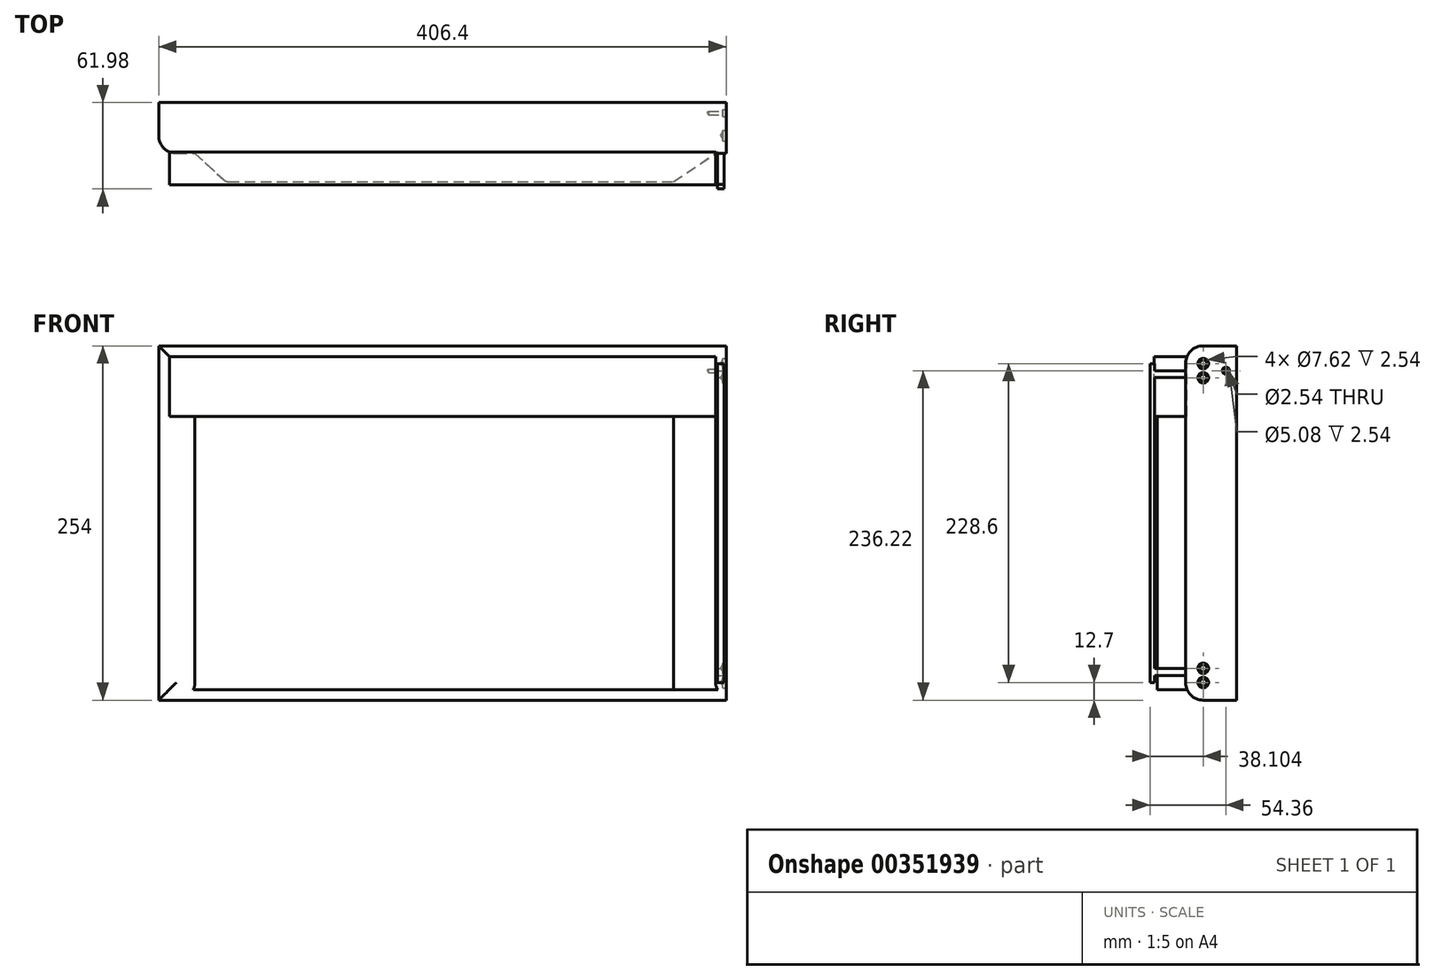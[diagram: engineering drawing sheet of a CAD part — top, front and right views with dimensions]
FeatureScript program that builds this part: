
annotation { "Feature Type Name" : "Feature", "Feature Type Description" : "" }
export const myFeature = defineFeature(function(context is Context, id is Id, definition is map)
    precondition{}
    {
        {
            var Q0;
            Q0=qCreatedBy(makeId("Front.planeOp"),FACE);
            var sketch = newSketch(context, id + "F0", { "sketchPlane" : qUnion([Q0])});
            skLineSegment(sketch, "E0.bottom", {"start": v(0, 0) * mm, "end": v(-406.4, 0) * mm});
            skLineSegment(sketch, "E0.top", {"start": v(0, -254) * mm, "end": v(-406.4, -254) * mm});
            skLineSegment(sketch, "E0.left", {"start": v(0, 0) * mm, "end": v(0, -254) * mm});
            skLineSegment(sketch, "E0.right", {"start": v(-406.4, 0) * mm, "end": v(-406.4, -254) * mm});
            skSolve(sketch);
        }
        {
            var Q0;
            Q0=makeQuery(id+"F0.imprint","IMPRINT",FACE,{"disambiguationData":[TD([[makeQuery(id+"F0.imprint","IMPRINT",EDGE,{"derivedFrom":sQuery(id+"F0.wireOp",EDGE,"E0.bottom")}),1.0]])]});
            extrude(context, id + "F1", {"entities" : qUnion([Q0]), "depth" : 36.58 * mm});
        }
        {
            var Q0;
            Q0=makeQuery(id+"F1.opExtrude","CAP_FACE",FACE,{"disambiguationData":[OSD([sQuery(id+"F0.wireOp",EDGE,"E0.bottom"),sQuery(id+"F0.wireOp",EDGE,"E0.top"),sQuery(id+"F0.wireOp",EDGE,"E0.left"),sQuery(id+"F0.wireOp",EDGE,"E0.right")])],"isStart":false});
            var sketch = newSketch(context, id + "F2", { "sketchPlane" : qUnion([Q0])});
            skLineSegment(sketch, "E1", {"start": v(-398.78, -246.38) * mm, "end": v(-398.78, -7.62) * mm});
            skLineSegment(sketch, "E2", {"start": v(-398.78, -7.62) * mm, "end": v(-7.62, -7.62) * mm});
            skLineSegment(sketch, "E3", {"start": v(-398.78, -246.38) * mm, "end": v(-7.62, -246.38) * mm});
            skLineSegment(sketch, "E4", {"start": v(-7.62, -246.38) * mm, "end": v(-7.62, -7.62) * mm});
            skSolve(sketch);
        }
        {
            var Q0;
            Q0=makeQuery(id+"F2.imprint","IMPRINT",FACE,{"disambiguationData":[TD([[makeQuery(id+"F2.imprint","IMPRINT",EDGE,{"derivedFrom":sQuery(id+"F2.wireOp",EDGE,"E1")}),-1.0]])]});
            extrude(context, id + "F3", {"entities" : qUnion([Q0]), "operationType" : NewBodyOperationType.ADD, "depth" : 22.6 * mm});
        }
        {
            var Q0;
            Q0=makeQuery(id+"F3.opExtrude","SWEPT_FACE",FACE,{"disambiguationData":[OSD([sQuery(id+"F2.wireOp",EDGE,"E3")])]});
            var sketch = newSketch(context, id + "F4", { "sketchPlane" : qUnion([Q0])});
            skLineSegment(sketch, "E5", {"start": v(-380.42, 36.58) * mm, "end": v(-358.27, 56.85) * mm});
            skLineSegment(sketch, "E6", {"start": v(-358.27, 56.85) * mm, "end": v(-37.8, 56.85) * mm});
            skLineSegment(sketch, "E7", {"start": v(-37.8, 56.85) * mm, "end": v(-7.62, 36.58) * mm});
            skSolve(sketch);
        }
        {
            var Q0;
            {var subQ2=sQuery(id+"F4.wireOp",EDGE,"E5");Q0=makeQuery(id+"F4.imprint","IMPRINT",FACE,{"disambiguationData":[TD([[makeQuery(id+"F4.imprint","IMPRINT",EDGE,{"derivedFrom":subQ2}),1.0]])]});}
            extrude(context, id + "F5", {"entities" : qUnion([Q0]), "operationType" : NewBodyOperationType.REMOVE, "oppositeDirection" : true, "depth" : 195.83 * mm});
        }
        {
            var Q0;
            Q0=makeQuery(id+"F5.boolean.opBoolean","COPY",EDGE,{"derivedFrom":makeQuery(id+"F5.opExtrude","CAP_EDGE",EDGE,{"disambiguationData":[OSD([sQuery(id+"F4.wireOp",EDGE,"E6")])],"isStart":true})});
            var Q1;
            Q1=makeQuery(id+"F5.boolean.opBoolean","COPY",EDGE,{"derivedFrom":makeQuery(id+"F5.opExtrude","CAP_EDGE",EDGE,{"disambiguationData":[OSD([sQuery(id+"F4.wireOp",EDGE,"E5")])],"isStart":true})});
            var Q2;
            Q2=makeQuery(id+"F5.boolean.opBoolean","COPY",EDGE,{"derivedFrom":makeQuery(id+"F5.opExtrude","SWEPT_EDGE",EDGE,{"disambiguationData":[OSD([sQuery(id+"F4.wireOp",EDGE,"E5"),sQuery(id+"F4.wireOp",EDGE,"E6")])]})});
            var Q3;
            Q3=makeQuery(id+"F5.boolean.opBoolean","INTERSECT",EDGE,{"derivedFrom":[makeQuery(id+"F3.opExtrude","SWEPT_FACE",FACE,{"disambiguationData":[OSD([sQuery(id+"F2.wireOp",EDGE,"E2")])]}),makeQuery(id+"F5.opExtrude","SWEPT_FACE",FACE,{"disambiguationData":[OSD([sQuery(id+"F4.wireOp",EDGE,"E5")])]})]});
            var Q4;
            Q4=makeQuery(id+"F5.boolean.opBoolean","INTERSECT",EDGE,{"derivedFrom":[makeQuery(id+"F3.opExtrude","SWEPT_FACE",FACE,{"disambiguationData":[OSD([sQuery(id+"F2.wireOp",EDGE,"E2")])]}),makeQuery(id+"F5.opExtrude","SWEPT_FACE",FACE,{"disambiguationData":[OSD([sQuery(id+"F4.wireOp",EDGE,"E6")])]})]});
            var Q5;
            {var subQ0=sQuery(id+"F7NSI61EkHc6LHw_1.wireOp",EDGE,"ORKUqMSw-jbk6-ItTb-sdrK-fpS0Z8fCi9uI");var subQ1=sQuery(id+"F7NSI61EkHc6LHw_1.wireOp",EDGE,"0TJsNva3-6Dh7-84AK-LeQ4-RBizLzSJ0fqv");var subQ2=sQuery(id+"F4.wireOp",EDGE,"E7");var subQ7=makeQuery(id+"F5.boolean.opBoolean","COPY",EDGE,{"derivedFrom":makeQuery(id+"F5.opExtrude","CAP_EDGE",EDGE,{"disambiguationData":[OSD([subQ2])],"isStart":true})});Q5=makeQuery(id+"FVFLB6VGkvuXAbx_1.boolean.opBoolean","MERGE",EDGE,{"derivedFrom":[makeQuery(id+"FeTA0CBMJBVCges_1.boolean.opBoolean","SPLIT",EDGE,{"disambiguationData":[TD([makeQuery(id+"FeTA0CBMJBVCges_1.opExtrude","SWEPT_FACE",FACE,{"disambiguationData":[OSD([subQ1])]})])],"derivedFrom":subQ7}),makeQuery(id+"FeTA0CBMJBVCges_1.boolean.opBoolean","SPLIT",EDGE,{"disambiguationData":[TD([makeQuery(id+"F5.boolean.opBoolean","COPY",FACE,{"derivedFrom":makeQuery(id+"F5.opExtrude","SWEPT_FACE",FACE,{"disambiguationData":[OSD([sQuery(id+"F4.wireOp",EDGE,"E6")])]})})])],"derivedFrom":subQ7}),makeQuery(id+"FVFLB6VGkvuXAbx_1.opExtrude","SWEPT_EDGE",EDGE,{"disambiguationData":[OSD([subQ2,subQ1,subQ0])]})]});}
            var Q6;
            {var subQ0=sQuery(id+"F7NSI61EkHc6LHw_1.wireOp",EDGE,"0TJsNva3-6Dh7-84AK-LeQ4-RBizLzSJ0fqv");var subQ1=sQuery(id+"F7NSI61EkHc6LHw_1.wireOp",EDGE,"UkR4Pr4L-OhKx-Odhu-bI6Y-4uwR8GJGrYWx");var subQ2=sQuery(id+"F4.wireOp",EDGE,"E7");var subQ3=sQuery(id+"F2.wireOp",EDGE,"E2");var subQ4=makeQuery(id+"F5.opExtrude","SWEPT_FACE",FACE,{"disambiguationData":[OSD([subQ2])]});var subQ6=makeQuery(id+"F3.opExtrude","SWEPT_FACE",FACE,{"disambiguationData":[OSD([subQ3])]});var subQ8=makeQuery(id+"F5.boolean.opBoolean","INTERSECT",EDGE,{"derivedFrom":[subQ6,subQ4]});Q6=makeQuery(id+"FVFLB6VGkvuXAbx_1.boolean.opBoolean","MERGE",EDGE,{"derivedFrom":[makeQuery(id+"FeTA0CBMJBVCges_1.boolean.opBoolean","SPLIT",EDGE,{"disambiguationData":[TD([makeQuery(id+"FeTA0CBMJBVCges_1.opExtrude","SWEPT_FACE",FACE,{"disambiguationData":[OSD([subQ0])]})])],"derivedFrom":subQ8}),makeQuery(id+"FeTA0CBMJBVCges_1.boolean.opBoolean","SPLIT",EDGE,{"disambiguationData":[TD([makeQuery(id+"F5.boolean.opBoolean","COPY",FACE,{"derivedFrom":makeQuery(id+"F5.opExtrude","SWEPT_FACE",FACE,{"disambiguationData":[OSD([sQuery(id+"F4.wireOp",EDGE,"E6")])]})})])],"derivedFrom":subQ8}),makeQuery(id+"FVFLB6VGkvuXAbx_1.opExtrude","SWEPT_EDGE",EDGE,{"disambiguationData":[OSD([subQ3,subQ2,subQ1,subQ0])]})]});}
            var Q7;
            Q7=makeQuery(id+"FeTA0CBMJBVCges_1.opExtrude","CAP_EDGE",EDGE,{"disambiguationData":[OSD([sQuery(id+"F7NSI61EkHc6LHw_1.wireOp",EDGE,"ORKUqMSw-jbk6-ItTb-sdrK-fpS0Z8fCi9uI")])],"isStart":false});
            var Q8;
            Q8=makeQuery(id+"FeTA0CBMJBVCges_1.opExtrude","CAP_EDGE",EDGE,{"disambiguationData":[OSD([sQuery(id+"F7NSI61EkHc6LHw_1.wireOp",EDGE,"UkR4Pr4L-OhKx-Odhu-bI6Y-4uwR8GJGrYWx")])],"isStart":false});
            var Q9;
            Q9=makeQuery(id+"FVFLB6VGkvuXAbx_1.boolean.opBoolean","COPY",EDGE,{"derivedFrom":makeQuery(id+"FVFLB6VGkvuXAbx_1.opExtrude","CAP_EDGE",EDGE,{"disambiguationData":[OSD([sQuery(id+"FHyrUoYh2R4RpAu_1.wireOp",EDGE,"adAzwLTH-pLZ5-psXU-4rEc-LQfEqqFDtrXA")])],"isStart":true})});
            var Q10;
            Q10=makeQuery(id+"FVFLB6VGkvuXAbx_1.boolean.opBoolean","INTERSECT",EDGE,{"derivedFrom":[makeQuery(id+"FeTA0CBMJBVCges_1.opExtrude","SWEPT_FACE",FACE,{"disambiguationData":[OSD([sQuery(id+"F7NSI61EkHc6LHw_1.wireOp",EDGE,"5KaXzMR0-0uw7-bbEw-IDZP-VAOk332MkSHk")])]}),makeQuery(id+"FVFLB6VGkvuXAbx_1.opExtrude","SWEPT_FACE",FACE,{"disambiguationData":[OSD([sQuery(id+"FHyrUoYh2R4RpAu_1.wireOp",EDGE,"adAzwLTH-pLZ5-psXU-4rEc-LQfEqqFDtrXA")])]})]});
            var Q11;
            Q11=makeQuery(id+"FVFLB6VGkvuXAbx_1.boolean.opBoolean","COPY",EDGE,{"derivedFrom":makeQuery(id+"FVFLB6VGkvuXAbx_1.opExtrude","CAP_EDGE",EDGE,{"disambiguationData":[OSD([sQuery(id+"FHyrUoYh2R4RpAu_1.wireOp",EDGE,"d7eemTo3-4muD-epPD-79P2-bkFwu8YvylHP")])],"isStart":true})});
            var Q12;
            Q12=makeQuery(id+"FVFLB6VGkvuXAbx_1.boolean.opBoolean","INTERSECT",EDGE,{"derivedFrom":[makeQuery(id+"FeTA0CBMJBVCges_1.opExtrude","SWEPT_FACE",FACE,{"disambiguationData":[OSD([sQuery(id+"F7NSI61EkHc6LHw_1.wireOp",EDGE,"5KaXzMR0-0uw7-bbEw-IDZP-VAOk332MkSHk")])]}),makeQuery(id+"FVFLB6VGkvuXAbx_1.opExtrude","SWEPT_FACE",FACE,{"disambiguationData":[OSD([sQuery(id+"FHyrUoYh2R4RpAu_1.wireOp",EDGE,"d7eemTo3-4muD-epPD-79P2-bkFwu8YvylHP")])]})]});
            fillet(context, id + "F6", {"entities" : qUnion([Q0, Q1, Q2, Q3, Q4, Q5, Q6, Q7, Q8, Q9, Q10, Q11, Q12]), "radius" : 5.08 * mm, "tangentPropagation" : true, "allowEdgeOverflow" : false});
        }
        {
            var Q0;
            Q0=makeQuery(id+"F1.opExtrude","CAP_EDGE",EDGE,{"disambiguationData":[OSD([sQuery(id+"F0.wireOp",EDGE,"E0.top")])],"isStart":false});
            var Q1;
            Q1=makeQuery(id+"F1.opExtrude","CAP_EDGE",EDGE,{"disambiguationData":[OSD([sQuery(id+"F0.wireOp",EDGE,"E0.bottom")])],"isStart":false});
            var Q2;
            Q2=makeQuery(id+"F1.opExtrude","CAP_EDGE",EDGE,{"disambiguationData":[OSD([sQuery(id+"F0.wireOp",EDGE,"E0.right")])],"isStart":false});
            fillet(context, id + "F7", {"entities" : qUnion([Q0, Q1, Q2]), "radius" : 12.7 * mm, "tangentPropagation" : true, "allowEdgeOverflow" : false});
        }
        {
            var Q0;
            Q0=makeQuery(id+"F1.opExtrude","SWEPT_FACE",FACE,{"disambiguationData":[OSD([sQuery(id+"F0.wireOp",EDGE,"E0.left")])]});
            var sketch = newSketch(context, id + "F8", { "sketchPlane" : qUnion([Q0])});
            skPoint(sketch, "E8", {"position": v(-23.88, -241.3) * mm});
            skPoint(sketch, "E9", {"position": v(-23.88, -12.7) * mm});
            skPoint(sketch, "E10", {"position": v(-23.88, -22.86) * mm});
            skPoint(sketch, "E11", {"position": v(-23.88, -231.14) * mm});
            skSolve(sketch);
        }
        {
            var Q0;
            Q0=sQuery(id+"F8.wireOp",VERTEX,"E8");
            var Q1;
            Q1=sQuery(id+"F8.wireOp",VERTEX,"E11");
            var Q2;
            Q2=sQuery(id+"F8.wireOp",VERTEX,"E10");
            var Q3;
            Q3=sQuery(id+"F8.wireOp",VERTEX,"E9");
            var Q4;
            Q4=makeQuery(id+"F1.opExtrude","SWEPT_BODY",BODY,{"disambiguationData":[OSD([sQuery(id+"F0.wireOp",EDGE,"E0.bottom"),sQuery(id+"F0.wireOp",EDGE,"E0.top"),sQuery(id+"F0.wireOp",EDGE,"E0.left"),sQuery(id+"F0.wireOp",EDGE,"E0.right")])]});
            hole(context, id + "F9", {"style" : HoleStyle.C_BORE, "endStyle" : HoleEndStyle.BLIND, "holeDiameter" : 5.08 * mm, "cBoreDiameter" : 7.62 * mm, "cBoreDepth" : 2.54 * mm, "holeDepth" : 2.54 * mm, "isTappedThrough" : true, "tappedDepth" : 12.7 * mm, "tapClearance" : 3, "locations" : qUnion([Q0, Q1, Q2, Q3]), "scope" : qUnion([Q4])});
        }
        {
            var Q0;
            Q0=makeQuery(id+"F1.opExtrude","SWEPT_FACE",FACE,{"disambiguationData":[OSD([sQuery(id+"F0.wireOp",EDGE,"E0.left")])]});
            var sketch = newSketch(context, id + "F10", { "sketchPlane" : qUnion([Q0])});
            skPoint(sketch, "E12", {"position": v(-7.62, -17.78) * mm});
            skSolve(sketch);
        }
        {
            var Q0;
            Q0=sQuery(id+"F10.wireOp",VERTEX,"E12");
            var Q1;
            Q1=makeQuery(id+"F1.opExtrude","SWEPT_BODY",BODY,{"disambiguationData":[OSD([sQuery(id+"F0.wireOp",EDGE,"E0.bottom"),sQuery(id+"F0.wireOp",EDGE,"E0.top"),sQuery(id+"F0.wireOp",EDGE,"E0.left"),sQuery(id+"F0.wireOp",EDGE,"E0.right")])]});
            hole(context, id + "F11", {"style" : HoleStyle.C_BORE, "endStyle" : HoleEndStyle.BLIND, "holeDiameter" : 2.54 * mm, "cBoreDiameter" : 5.08 * mm, "cBoreDepth" : 2.54 * mm, "holeDepth" : 12.7 * mm, "isTappedThrough" : true, "tappedDepth" : 12.7 * mm, "tapClearance" : 3, "locations" : qUnion([Q0]), "scope" : qUnion([Q1])});
        }
        {
            var Q0;
            {var subQ0=sQuery(id+"F2.wireOp",EDGE,"E3");var subQ1=makeQuery(id+"F3.opExtrude","CAP_EDGE",EDGE,{"disambiguationData":[OSD([subQ0])],"isStart":true});Q0=makeQuery(id+"F7.opFillet","SPLIT",FACE,{"disambiguationData":[OD(0.0)],"derivedFrom":makeQuery(id+"F5.boolean.opBoolean","MERGE",FACE,{"derivedFrom":[makeQuery(id+"F1.opExtrude","CAP_FACE",FACE,{"disambiguationData":[OSD([sQuery(id+"F0.wireOp",EDGE,"E0.bottom"),sQuery(id+"F0.wireOp",EDGE,"E0.top"),sQuery(id+"F0.wireOp",EDGE,"E0.left"),sQuery(id+"F0.wireOp",EDGE,"E0.right")])],"isStart":false}),makeQuery(id+"F5.opExtrude","SWEPT_FACE",FACE,{"disambiguationData":[OSD([subQ0]),TDD([makeQuery(id+"F4.imprint","IMPRINT",EDGE,{"disambiguationData":[TD([[makeQuery(id+"F4.imprint","INTERSECT",VERTEX,{"derivedFrom":[subQ1,sQuery(id+"F4.wireOp",EDGE,"E5")]}),1.0]])],"derivedFrom":subQ1})])]})]})});}
            var sketch = newSketch(context, id + "F12", { "sketchPlane" : qUnion([Q0])});
            skLineSegment(sketch, "E13", {"start": v(-1.35, -241.3) * mm, "end": v(-1.35, -12.7) * mm});
            skPoint(sketch, "E13.endSnap0", {"position": v(-3.81, -12.7) * mm});
            skLineSegment(sketch, "E14", {"start": v(-1.35, -12.7) * mm, "end": v(-6.39, -12.7) * mm});
            skLineSegment(sketch, "E15", {"start": v(-6.39, -12.7) * mm, "end": v(-6.39, -241.3) * mm});
            skPoint(sketch, "E15.endSnap0", {"position": v(-3.8, -241.3) * mm});
            skLineSegment(sketch, "E16", {"start": v(-6.39, -241.3) * mm, "end": v(-1.35, -241.3) * mm});
            skSolve(sketch);
        }
        {
            var Q0;
            Q0=makeQuery(id+"F12.imprint","IMPRINT",FACE,{"disambiguationData":[TD([[makeQuery(id+"F12.imprint","IMPRINT",EDGE,{"derivedFrom":sQuery(id+"F12.wireOp",EDGE,"E13")}),1.0]])]});
            extrude(context, id + "F13", {"entities" : qUnion([Q0]), "operationType" : NewBodyOperationType.ADD, "depth" : 25.4 * mm});
        }
        {
            var Q0;
            Q0=makeQuery(id+"F13.opExtrude","SWEPT_FACE",FACE,{"disambiguationData":[OSD([sQuery(id+"F12.wireOp",EDGE,"E13")])]});
            var sketch = newSketch(context, id + "F14", { "sketchPlane" : qUnion([Q0])});
            skLineSegment(sketch, "E17", {"start": v(-36.58, -236.22) * mm, "end": v(-58.76, -236.22) * mm});
            skLineSegment(sketch, "E18", {"start": v(-58.76, -236.22) * mm, "end": v(-58.76, -241.3) * mm});
            skLineSegment(sketch, "E19", {"start": v(-36.58, -231.4) * mm, "end": v(-58.76, -231.4) * mm});
            skLineSegment(sketch, "E20", {"start": v(-58.76, -231.4) * mm, "end": v(-58.76, -22.6) * mm});
            skLineSegment(sketch, "E21", {"start": v(-58.76, -22.6) * mm, "end": v(-36.58, -22.6) * mm});
            skLineSegment(sketch, "E22", {"start": v(-36.58, -22.6) * mm, "end": v(-36.58, -17.78) * mm});
            skLineSegment(sketch, "E23", {"start": v(-36.58, -17.78) * mm, "end": v(-58.76, -17.78) * mm});
            skLineSegment(sketch, "E24", {"start": v(-58.76, -17.78) * mm, "end": v(-58.76, -12.7) * mm});
            skSolve(sketch);
        }
        {
            var Q0;
            {var subQ0=sQuery(id+"F14.wireOp",EDGE,"E19");Q0=makeQuery(id+"F14.imprint","IMPRINT",FACE,{"disambiguationData":[TD([[makeQuery(id+"F14.imprint","IMPRINT",EDGE,{"derivedFrom":subQ0}),-1.0]])]});}
            var Q1;
            {var subQ0=sQuery(id+"F14.wireOp",EDGE,"E17");Q1=makeQuery(id+"F14.imprint","IMPRINT",FACE,{"disambiguationData":[TD([[makeQuery(id+"F14.imprint","IMPRINT",EDGE,{"derivedFrom":subQ0}),1.0]])]});}
            var Q2;
            {var subQ0=sQuery(id+"F14.wireOp",EDGE,"E23");Q2=makeQuery(id+"F14.imprint","IMPRINT",FACE,{"disambiguationData":[TD([[makeQuery(id+"F14.imprint","IMPRINT",EDGE,{"derivedFrom":subQ0}),-1.0]])]});}
            extrude(context, id + "F15", {"entities" : qUnion([Q0, Q1, Q2]), "operationType" : NewBodyOperationType.REMOVE, "oppositeDirection" : true, "depth" : 5.84 * mm});
        }
    });
